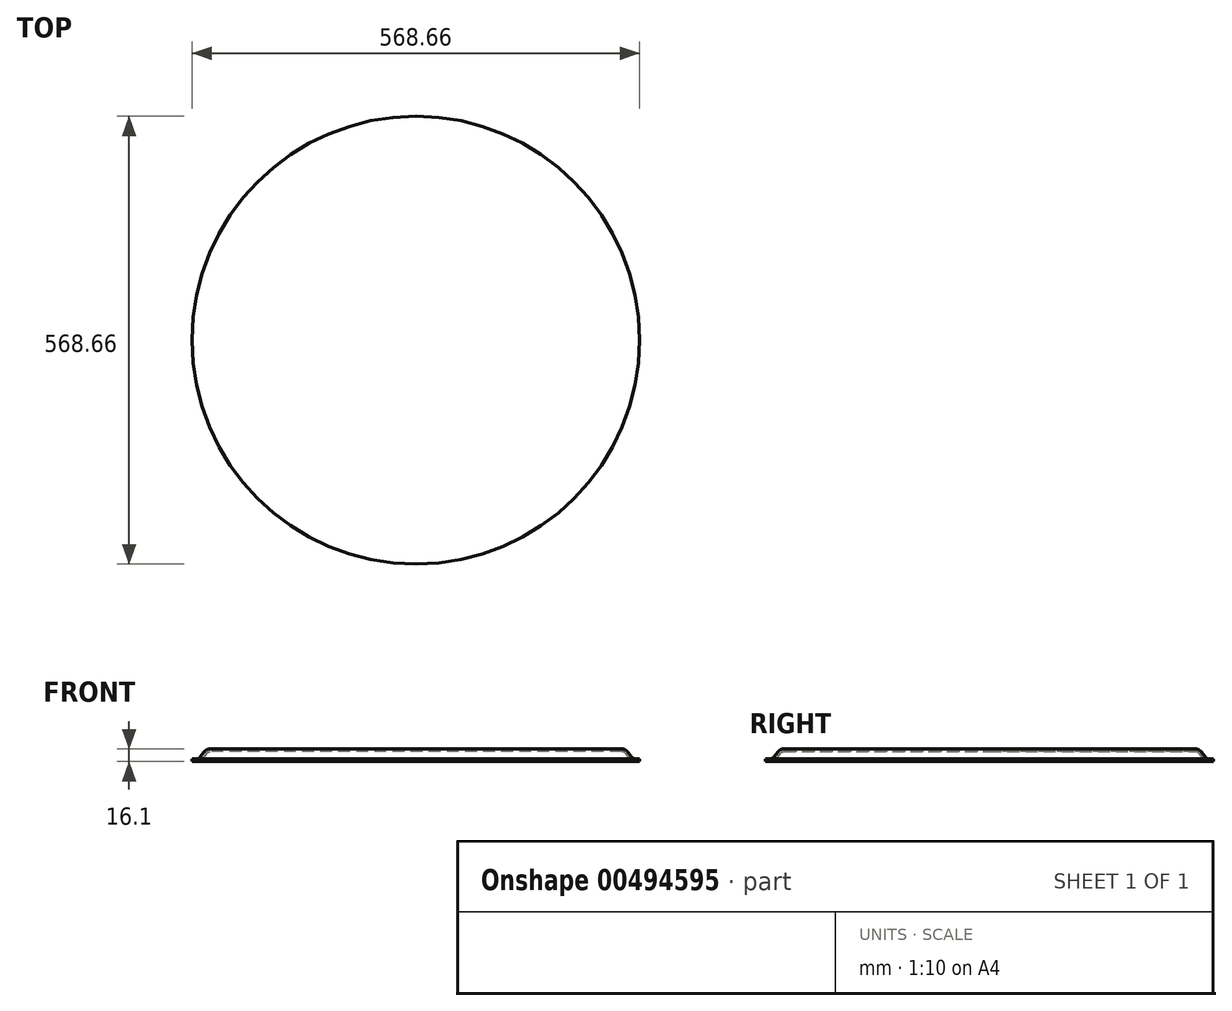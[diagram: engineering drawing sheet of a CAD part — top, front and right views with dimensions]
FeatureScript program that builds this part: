
annotation { "Feature Type Name" : "Feature", "Feature Type Description" : "" }
export const myFeature = defineFeature(function(context is Context, id is Id, definition is map)
    precondition{}
    {
        {
            var Q0;
            Q0=qCreatedBy(makeId("Front.planeOp"),FACE);
            var sketch = newSketch(context, id + "F0", { "sketchPlane" : qUnion([Q0])});
            skLineSegment(sketch, "E0", {"start": v(0, 0) * mm, "end": v(-261.34, 0) * mm});
            skLineSegment(sketch, "E1", {"start": v(-268.82, -3.63) * mm, "end": v(-274.06, -10.28) * mm});
            skLineSegment(sketch, "E2", {"start": v(-279.05, -12.7) * mm, "end": v(-284.33, -12.7) * mm});
            skPoint(sketch, "E3.visualSharp", {"position": v(-265.96, 0) * mm});
            skArc(sketch, "E3.filletArc", {"start": v(-261.34, 0) * mm, "mid": v(-265.5, -0.95) * mm, "end": v(-268.82, -3.63) * mm});
            skPoint(sketch, "E4.visualSharp", {"position": v(-275.97, -12.7) * mm});
            skArc(sketch, "E4.filletArc", {"start": v(-279.05, -12.7) * mm, "mid": v(-276.28, -12.06) * mm, "end": v(-274.06, -10.28) * mm});
            skLineSegment(sketch, "E5.0", {"start": v(-279.05, -16.1) * mm, "end": v(-284.33, -16.1) * mm});
            skLineSegment(sketch, "E5.1", {"start": v(0, -3.4) * mm, "end": v(-261.34, -3.4) * mm});
            skArc(sketch, "E5.2", {"start": v(-261.34, -3.4) * mm, "mid": v(-264, -4.02) * mm, "end": v(-266.15, -5.74) * mm});
            skLineSegment(sketch, "E5.3", {"start": v(-266.15, -5.74) * mm, "end": v(-271.4, -12.39) * mm});
            skArc(sketch, "E5.4", {"start": v(-279.05, -16.1) * mm, "mid": v(-274.8, -15.13) * mm, "end": v(-271.4, -12.39) * mm});
            skLineSegment(sketch, "E6", {"start": v(-284.33, -12.7) * mm, "end": v(-284.33, -16.1) * mm});
            skLineSegment(sketch, "E7", {"start": v(0, 0) * mm, "end": v(0, -3.4) * mm});
            skSolve(sketch);
        }
        {
            var Q0;
            Q0=qSketchRegion(id+"F0",true);
            var Q1;
            Q1=sQuery(id+"F0.wireOp",EDGE,"E7");
            revolve(context, id + "F1", {"entities" : qUnion([Q0]), "axis" : qUnion([Q1]), "revolveType" : RevolveType.FULL});
        }
    });
